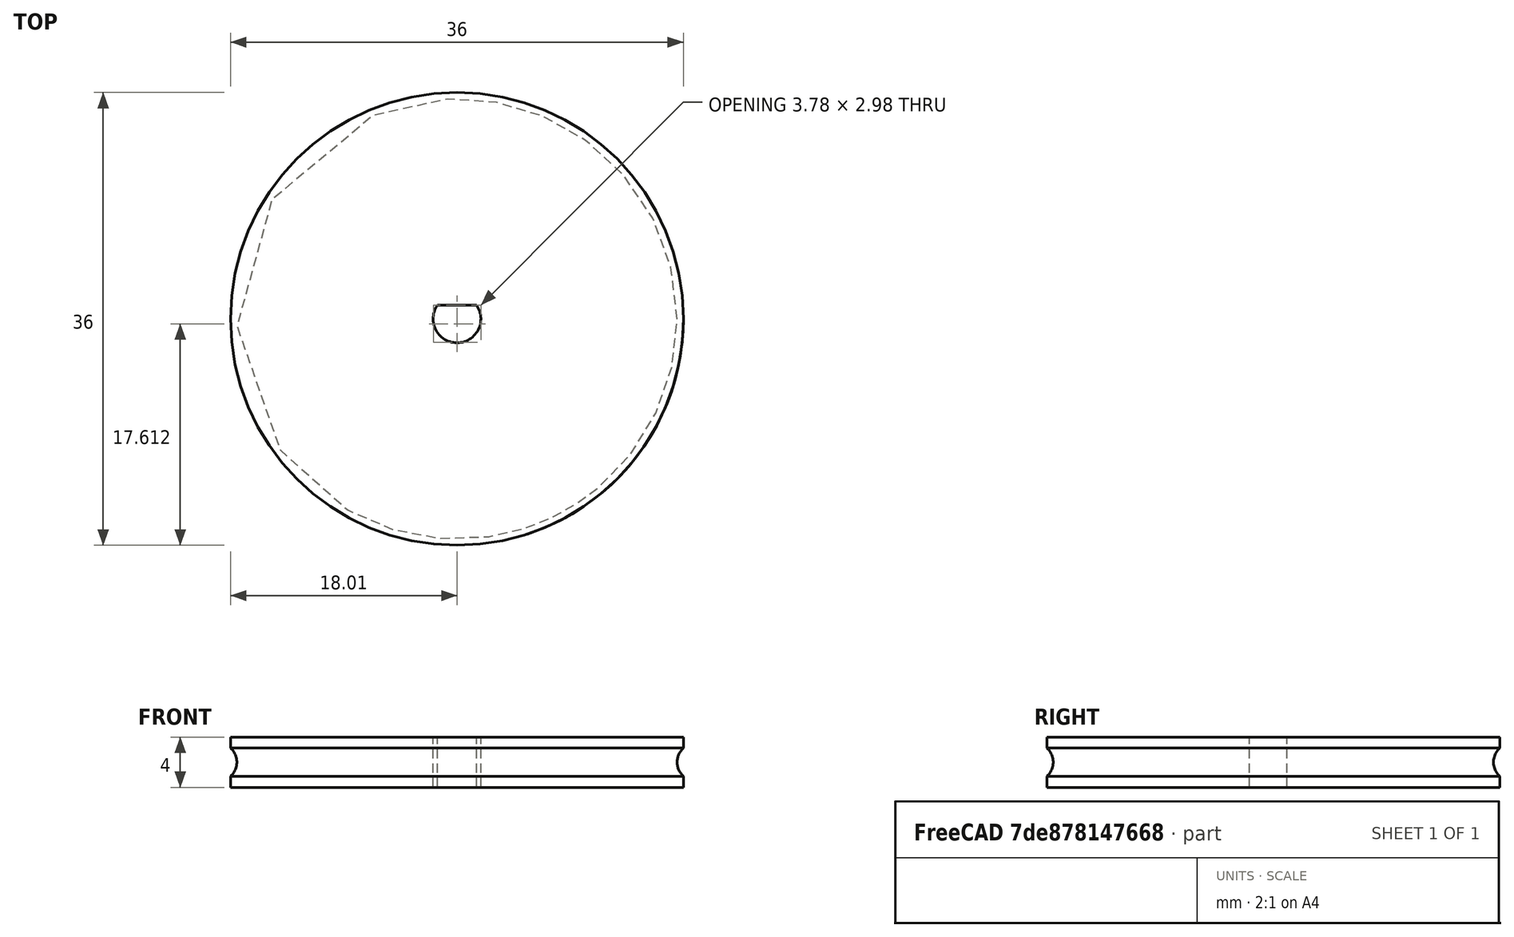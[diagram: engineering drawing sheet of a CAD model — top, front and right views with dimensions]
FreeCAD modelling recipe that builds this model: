
FCSTD DOCUMENT  (FreeCAD 0.16R6703 (Git))
Label: wheel
License: All rights reserved
LicenseURL: http://en.wikipedia.org/wiki/All_rights_reserved
objects: Part::Cut×3, Part::Cylinder×2, Part::Box×1, Part::Torus×1
note: 7 computed .brp shape members not serialized (recipe doc carries the construction recipe); baked Part::Feature solids carry a one-line shape summary decoded from their .brp

FEATURE [Part::Cylinder] Cylinder012  label="wheel1a"
  Angle = 360
  Height = 4
  Radius = 18
FEATURE [Part::Cylinder] Cylinder028  label="Cylinder024"
  Angle = 360
  Height = 10
  Placement = pos=(0,0,-1) rot=(0,0,1;0rad)
  Radius = 1.9
FEATURE [Part::Box] Box084016  label="Cube067"
  Height = 12
  Length = 10
  Placement = pos=(-5,1.1,-1.5) rot=(0,0,1;0rad)
  Width = 10
FEATURE [Part::Cut] Cut057
  Base = -> Cylinder028
  Tool = -> Box084016
FEATURE [Part::Cut] Cut062
  Base = -> Cylinder012
  Tool = -> Cut057
FEATURE [Part::Torus] Torus002
  Angle1 = -180
  Angle2 = 180
  Angle3 = 360
  Placement = pos=(0,0,2) rot=(0,0,1;0rad)
  Radius1 = 19
  Radius2 = 1.5
FEATURE [Part::Cut] Cut063  label="wheel"
  Base = -> Cut062
  Placement = pos=(0,-20,48) rot=(0,0,1;0rad)
  Tool = -> Torus002
